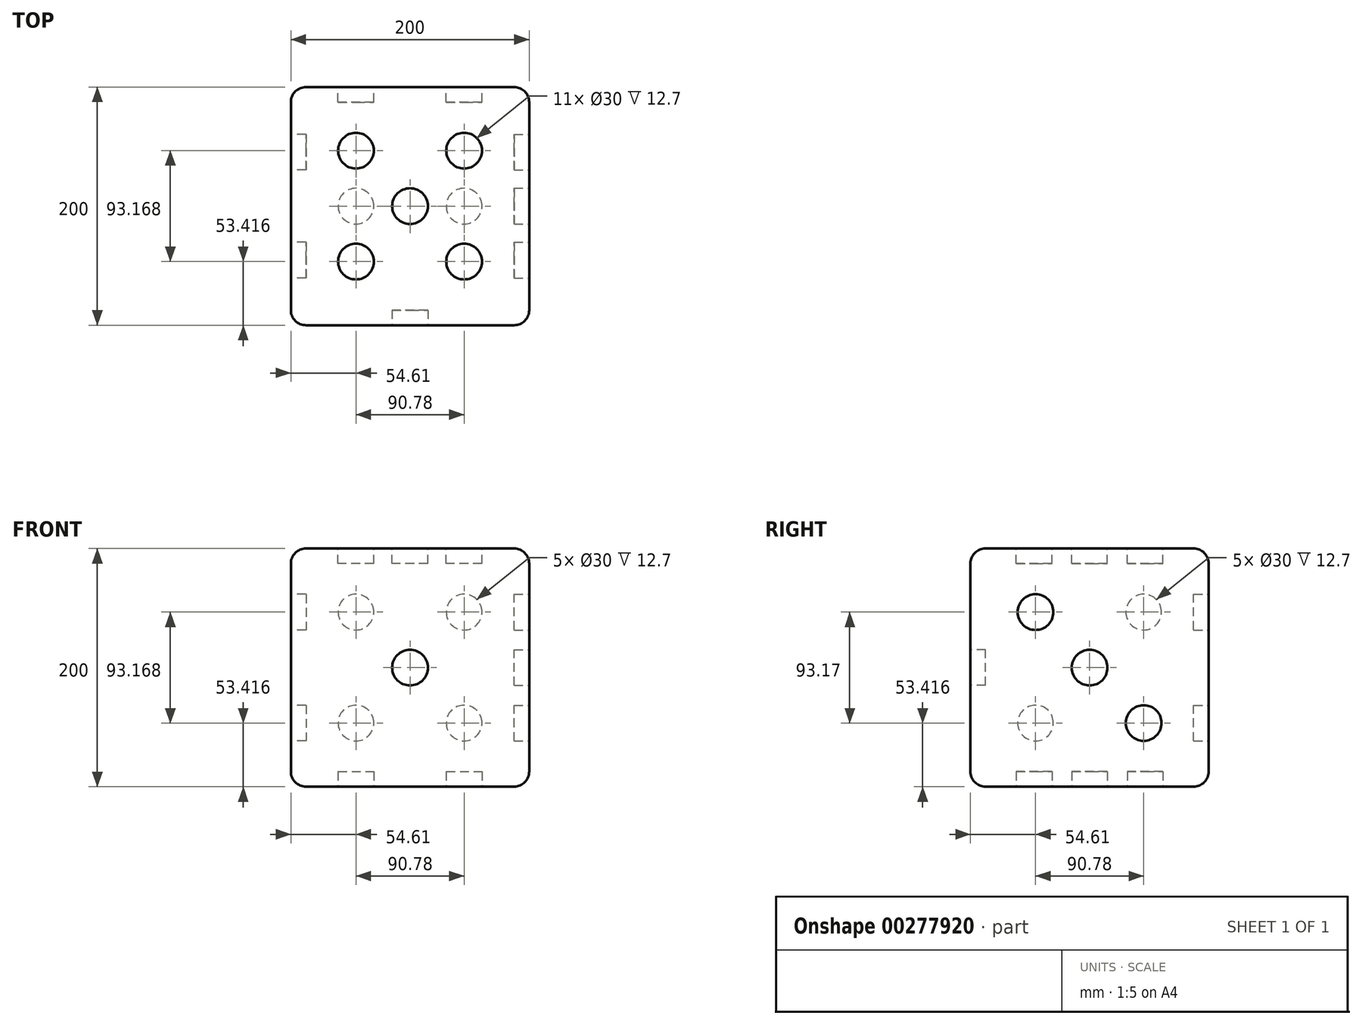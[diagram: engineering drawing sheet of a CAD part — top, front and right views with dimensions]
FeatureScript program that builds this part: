
annotation { "Feature Type Name" : "Feature", "Feature Type Description" : "" }
export const myFeature = defineFeature(function(context is Context, id is Id, definition is map)
    precondition{}
    {
        {
            var Q0;
            Q0=qCreatedBy(makeId("Front.planeOp"),FACE);
            var sketch = newSketch(context, id + "F0", { "sketchPlane" : qUnion([Q0])});
            skLineSegment(sketch, "E0.bottom", {"start": v(100, -100) * mm, "end": v(-100, -100) * mm});
            skLineSegment(sketch, "E0.top", {"start": v(100, 100) * mm, "end": v(-100, 100) * mm});
            skLineSegment(sketch, "E0.left", {"start": v(100, -100) * mm, "end": v(100, 100) * mm});
            skLineSegment(sketch, "E0.right", {"start": v(-100, -100) * mm, "end": v(-100, 100) * mm});
            skPoint(sketch, "E0.middle", {"position": v(0, 0) * mm});
            skSolve(sketch);
        }
        {
            var Q0;
            Q0=makeQuery(id+"F0.imprint","IMPRINT",FACE,{"disambiguationData":[TD([[makeQuery(id+"F0.imprint","IMPRINT",EDGE,{"derivedFrom":sQuery(id+"F0.wireOp",EDGE,"E0.bottom")}),-1.0]])]});
            extrude(context, id + "F1", {"entities" : qUnion([Q0]), "depth" : 200 * mm});
        }
        {
            var Q0;
            Q0=makeQuery(id+"F1.opExtrude","CAP_EDGE",EDGE,{"disambiguationData":[OSD([sQuery(id+"F0.wireOp",EDGE,"E0.top")])],"isStart":false});
            var Q1;
            Q1=makeQuery(id+"F1.opExtrude","SWEPT_EDGE",EDGE,{"disambiguationData":[OSD([sQuery(id+"F0.wireOp",EDGE,"E0.top"),sQuery(id+"F0.wireOp",EDGE,"E0.left")])]});
            var Q2;
            Q2=makeQuery(id+"F1.opExtrude","SWEPT_EDGE",EDGE,{"disambiguationData":[OSD([sQuery(id+"F0.wireOp",EDGE,"E0.top"),sQuery(id+"F0.wireOp",EDGE,"E0.right")])]});
            var Q3;
            Q3=makeQuery(id+"F1.opExtrude","CAP_EDGE",EDGE,{"disambiguationData":[OSD([sQuery(id+"F0.wireOp",EDGE,"E0.right")])],"isStart":false});
            var Q4;
            Q4=makeQuery(id+"F1.opExtrude","CAP_EDGE",EDGE,{"disambiguationData":[OSD([sQuery(id+"F0.wireOp",EDGE,"E0.bottom")])],"isStart":false});
            var Q5;
            Q5=makeQuery(id+"F1.opExtrude","CAP_EDGE",EDGE,{"disambiguationData":[OSD([sQuery(id+"F0.wireOp",EDGE,"E0.left")])],"isStart":false});
            var Q6;
            Q6=makeQuery(id+"F1.opExtrude","SWEPT_EDGE",EDGE,{"disambiguationData":[OSD([sQuery(id+"F0.wireOp",EDGE,"E0.bottom"),sQuery(id+"F0.wireOp",EDGE,"E0.right")])]});
            var Q7;
            Q7=makeQuery(id+"F1.opExtrude","CAP_EDGE",EDGE,{"disambiguationData":[OSD([sQuery(id+"F0.wireOp",EDGE,"E0.top")])],"isStart":true});
            var Q8;
            Q8=makeQuery(id+"F1.opExtrude","CAP_EDGE",EDGE,{"disambiguationData":[OSD([sQuery(id+"F0.wireOp",EDGE,"E0.right")])],"isStart":true});
            var Q9;
            Q9=makeQuery(id+"F1.opExtrude","CAP_EDGE",EDGE,{"disambiguationData":[OSD([sQuery(id+"F0.wireOp",EDGE,"E0.bottom")])],"isStart":true});
            var Q10;
            Q10=makeQuery(id+"F1.opExtrude","SWEPT_FACE",FACE,{"disambiguationData":[OSD([sQuery(id+"F0.wireOp",EDGE,"E0.left")])]});
            fillet(context, id + "F2", {"entities" : qUnion([Q0, Q1, Q2, Q3, Q4, Q5, Q6, Q7, Q8, Q9, Q10]), "radius" : 12.7 * mm, "tangentPropagation" : true, "allowEdgeOverflow" : false});
        }
        {
            var Q0;
            Q0=makeQuery(id+"F1.opExtrude","CAP_FACE",FACE,{"disambiguationData":[OSD([sQuery(id+"F0.wireOp",EDGE,"E0.bottom"),sQuery(id+"F0.wireOp",EDGE,"E0.top"),sQuery(id+"F0.wireOp",EDGE,"E0.left"),sQuery(id+"F0.wireOp",EDGE,"E0.right")])],"isStart":false});
            var sketch = newSketch(context, id + "F3", { "sketchPlane" : qUnion([Q0])});
            skCircle(sketch, "E1", {"center": v(0, 0) * mm, "radius": 15 * mm});
            skSolve(sketch);
        }
        {
            var Q0;
            Q0=makeQuery(id+"F3.imprint","IMPRINT",FACE,{"disambiguationData":[TD([[makeQuery(id+"F3.imprint","IMPRINT",EDGE,{"derivedFrom":sQuery(id+"F3.wireOp",EDGE,"E1")}),1.0]])]});
            extrude(context, id + "F4", {"entities" : qUnion([Q0]), "operationType" : NewBodyOperationType.REMOVE, "oppositeDirection" : true, "depth" : 12.7 * mm});
        }
        {
            var Q0;
            Q0=makeQuery(id+"F1.opExtrude","SWEPT_FACE",FACE,{"disambiguationData":[OSD([sQuery(id+"F0.wireOp",EDGE,"E0.right")])]});
            var sketch = newSketch(context, id + "F5", { "sketchPlane" : qUnion([Q0])});
            skLineSegment(sketch, "E2", {"start": v(12.7, 46.59) * mm, "end": v(187.3, 46.59) * mm, "construction": true});
            skLineSegment(sketch, "E3", {"start": v(12.7, -46.58) * mm, "end": v(187.3, -46.58) * mm, "construction": true});
            skLineSegment(sketch, "E4", {"start": v(54.6, 87.3) * mm, "end": v(54.61, -87.3) * mm, "construction": true});
            skLineSegment(sketch, "E5", {"start": v(145.4, 87.3) * mm, "end": v(145.4, -87.3) * mm, "construction": true});
            skCircle(sketch, "E6", {"center": v(54.6, 46.59) * mm, "radius": 15 * mm});
            skCircle(sketch, "E7", {"center": v(145.4, -46.58) * mm, "radius": 15 * mm});
            skSolve(sketch);
        }
        {
            var Q0;
            Q0 = qSketchRegion(id + "F5", true);
            extrude(context, id + "F6", {"entities" : qUnion([Q0]), "operationType" : NewBodyOperationType.REMOVE, "oppositeDirection" : true, "depth" : 12.7 * mm});
        }
        {
            var Q0;
            Q0=makeQuery(id+"F1.opExtrude","SWEPT_FACE",FACE,{"disambiguationData":[OSD([sQuery(id+"F0.wireOp",EDGE,"E0.left")])]});
            var sketch = newSketch(context, id + "F7", { "sketchPlane" : qUnion([Q0])});
            skLineSegment(sketch, "E8", {"start": v(-187.3, 0) * mm, "end": v(-12.7, 0) * mm, "construction": true});
            skLineSegment(sketch, "E9", {"start": v(-187.3, 46.58) * mm, "end": v(-12.7, 46.58) * mm, "construction": true});
            skLineSegment(sketch, "E10", {"start": v(-187.3, -46.58) * mm, "end": v(-12.7, -46.58) * mm, "construction": true});
            skLineSegment(sketch, "E11", {"start": v(-145.4, 87.3) * mm, "end": v(-145.4, -87.3) * mm, "construction": true});
            skLineSegment(sketch, "E12", {"start": v(-100, 87.3) * mm, "end": v(-100, -87.3) * mm, "construction": true});
            skLineSegment(sketch, "E13", {"start": v(-54.61, 87.3) * mm, "end": v(-54.6, -87.3) * mm, "construction": true});
            skCircle(sketch, "E14", {"center": v(-145.4, 46.58) * mm, "radius": 15 * mm});
            skCircle(sketch, "E15", {"center": v(-100, 0) * mm, "radius": 15 * mm});
            skCircle(sketch, "E16", {"center": v(-54.6, -46.58) * mm, "radius": 15 * mm});
            skSolve(sketch);
        }
        {
            var Q0;
            Q0 = qSketchRegion(id + "F7", true);
            extrude(context, id + "F8", {"entities" : qUnion([Q0]), "operationType" : NewBodyOperationType.REMOVE, "oppositeDirection" : true, "depth" : 12.7 * mm});
        }
        {
            var Q0;
            Q0=makeQuery(id+"F0.imprint","IMPRINT",FACE,{"disambiguationData":[TD([[makeQuery(id+"F0.imprint","IMPRINT",EDGE,{"derivedFrom":sQuery(id+"F0.wireOp",EDGE,"E0.bottom")}),-1.0]])]});
            var sketch = newSketch(context, id + "F9", { "sketchPlane" : qUnion([Q0])});
            skLineSegment(sketch, "E17", {"start": v(45.39, 87.5) * mm, "end": v(45.4, -87.36) * mm, "construction": true});
            skLineSegment(sketch, "E18", {"start": v(87.33, -46.58) * mm, "end": v(-88.55, -46.58) * mm, "construction": true});
            skLineSegment(sketch, "E19", {"start": v(86.92, 46.58) * mm, "end": v(-86.52, 46.58) * mm, "construction": true});
            skLineSegment(sketch, "E20", {"start": v(-45.4, 85.9) * mm, "end": v(-45.4, -85.9) * mm, "construction": true});
            skCircle(sketch, "E21", {"center": v(45.39, 46.58) * mm, "radius": 15 * mm});
            skCircle(sketch, "E22", {"center": v(45.4, -46.58) * mm, "radius": 15 * mm});
            skCircle(sketch, "E23", {"center": v(-45.4, -46.58) * mm, "radius": 15 * mm});
            skCircle(sketch, "E24", {"center": v(-45.4, 46.58) * mm, "radius": 15 * mm});
            skSolve(sketch);
        }
        {
            var Q0;
            Q0 = qSketchRegion(id + "F9", true);
            extrude(context, id + "F10", {"entities" : qUnion([Q0]), "operationType" : NewBodyOperationType.REMOVE, "depth" : 12.7 * mm});
        }
        {
            var Q0;
            Q0=makeQuery(id+"F1.opExtrude","SWEPT_FACE",FACE,{"disambiguationData":[OSD([sQuery(id+"F0.wireOp",EDGE,"E0.top")])]});
            var sketch = newSketch(context, id + "F11", { "sketchPlane" : qUnion([Q0])});
            skLineSegment(sketch, "E25", {"start": v(-45.4, -12.7) * mm, "end": v(-45.39, -187.3) * mm, "construction": true});
            skLineSegment(sketch, "E26", {"start": v(0, -12.7) * mm, "end": v(0, -187.3) * mm, "construction": true});
            skLineSegment(sketch, "E27", {"start": v(45.39, -12.7) * mm, "end": v(45.4, -187.3) * mm, "construction": true});
            skLineSegment(sketch, "E28", {"start": v(-87.3, -100) * mm, "end": v(87.3, -100) * mm, "construction": true});
            skLineSegment(sketch, "E29", {"start": v(-87.3, -53.42) * mm, "end": v(87.3, -53.42) * mm, "construction": true});
            skLineSegment(sketch, "E30", {"start": v(-87.3, -146.58) * mm, "end": v(87.3, -146.58) * mm, "construction": true});
            skCircle(sketch, "E31", {"center": v(0, -100) * mm, "radius": 15 * mm});
            skCircle(sketch, "E32", {"center": v(-45.4, -53.42) * mm, "radius": 15 * mm});
            skCircle(sketch, "E33", {"center": v(45.39, -53.42) * mm, "radius": 15 * mm});
            skCircle(sketch, "E34", {"center": v(-45.39, -146.58) * mm, "radius": 15 * mm});
            skCircle(sketch, "E35", {"center": v(45.4, -146.58) * mm, "radius": 15 * mm});
            skSolve(sketch);
        }
        {
            var Q0;
            Q0 = qSketchRegion(id + "F11", true);
            extrude(context, id + "F12", {"entities" : qUnion([Q0]), "operationType" : NewBodyOperationType.REMOVE, "oppositeDirection" : true, "depth" : 12.7 * mm});
        }
        {
            var Q0;
            Q0=makeQuery(id+"F1.opExtrude","SWEPT_FACE",FACE,{"disambiguationData":[OSD([sQuery(id+"F0.wireOp",EDGE,"E0.bottom")])]});
            var sketch = newSketch(context, id + "F13", { "sketchPlane" : qUnion([Q0])});
            skLineSegment(sketch, "E36", {"start": v(87.3, 53.42) * mm, "end": v(-87.3, 53.42) * mm, "construction": true});
            skLineSegment(sketch, "E37", {"start": v(87.3, 100) * mm, "end": v(-87.3, 100) * mm, "construction": true});
            skLineSegment(sketch, "E38", {"start": v(87.3, 146.58) * mm, "end": v(-87.3, 146.58) * mm, "construction": true});
            skLineSegment(sketch, "E39", {"start": v(45.39, 12.7) * mm, "end": v(45.39, 187.3) * mm, "construction": true});
            skLineSegment(sketch, "E40", {"start": v(-45.4, 12.7) * mm, "end": v(-45.4, 187.3) * mm, "construction": true});
            skCircle(sketch, "E41", {"center": v(45.39, 53.42) * mm, "radius": 15 * mm});
            skCircle(sketch, "E42", {"center": v(45.39, 100) * mm, "radius": 15 * mm});
            skCircle(sketch, "E43", {"center": v(45.39, 146.58) * mm, "radius": 15 * mm});
            skCircle(sketch, "E44", {"center": v(-45.4, 53.42) * mm, "radius": 15 * mm});
            skCircle(sketch, "E45", {"center": v(-45.4, 100) * mm, "radius": 15 * mm});
            skCircle(sketch, "E46", {"center": v(-45.4, 146.58) * mm, "radius": 15 * mm});
            skSolve(sketch);
        }
        {
            var Q0;
            Q0 = qSketchRegion(id + "F13", true);
            extrude(context, id + "F14", {"entities" : qUnion([Q0]), "operationType" : NewBodyOperationType.REMOVE, "oppositeDirection" : true, "depth" : 12.7 * mm});
        }
    });
